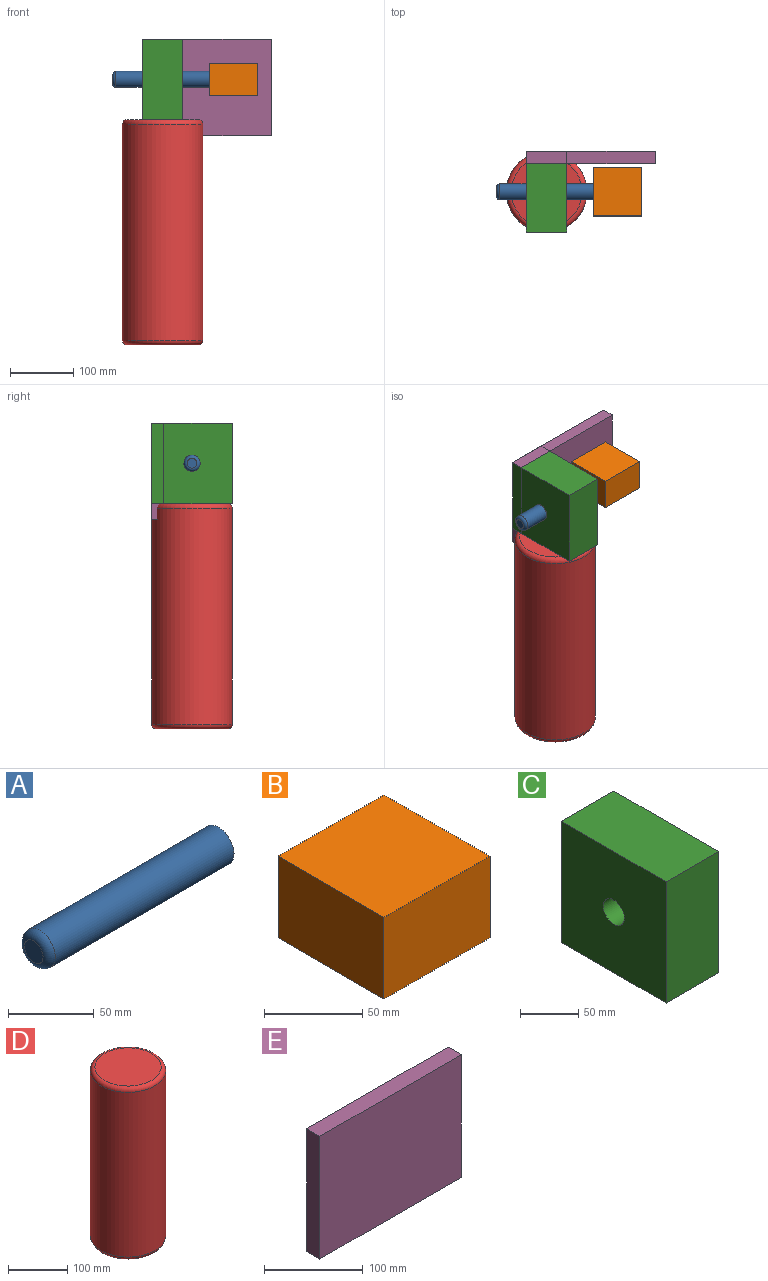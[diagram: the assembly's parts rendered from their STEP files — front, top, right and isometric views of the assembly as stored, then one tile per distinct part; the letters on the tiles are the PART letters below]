
ASSEMBLY  parts=5 mates=4
PART A: 4 faces, bbox 152.4x27.5x27.5 mm
  f0: cylinder r=12.7mm len=147.32mm, axis (-1,0,0), area 11755.6mm2, adj f1,f3
  f1: plane 25.4x25.4mm, normal (1,0,0), area 506.7mm2, adj f0
  f2: plane 15.24x15.24mm, normal (-1,0,0), area 182.4mm2, adj f3
  f3: torus R=7.62mm, axis (1,0,0), area 544.2mm2, adj f0,f2
PART B: 11 faces, bbox 76.2x76.2x50.8 mm
  f0: plane 76.2x50.8mm, normal (1,0,0), area 1703.2mm2, adj f1,f2,f4,f5,f6,f7,f8,f9
  f1: plane 76.2x76.2mm, normal (0,0,-1), area 5806.4mm2, adj f0,f3,f4,f5
  f2: plane 76.2x76.2mm, normal (0,0,1), area 5806.4mm2, adj f0,f3,f4,f5
  f3: plane 76.2x50.8mm, normal (-1,0,0), area 3871mm2, adj f1,f2,f4,f5
  f4: plane 76.2x50.8mm, normal (0,-1,0), area 3871mm2, adj f0,f1,f2,f3
  f5: plane 76.2x50.8mm, normal (0,1,0), area 3871mm2, adj f0,f1,f2,f3
  f6: plane 60.96x50.8mm, normal (0,0,1), area 3096.8mm2, adj f0,f7,f9,f10
  f7: plane 50.8x35.56mm, normal (0,-1,0), area 1806.4mm2, adj f0,f6,f8,f10
  f8: plane 60.96x50.8mm, normal (0,0,-1), area 3096.8mm2, adj f0,f7,f9,f10
  f9: plane 50.8x35.56mm, normal (0,1,0), area 1806.4mm2, adj f0,f6,f8,f10
  f10: plane 60.96x35.56mm, normal (1,0,0), area 2167.7mm2, adj f6,f7,f8,f9
PART C: 7 faces, bbox 63.5x127x127 mm
  f0: plane 127x127mm, normal (-1,0,0), area 15622.3mm2, adj f1,f3,f4,f5,f6
  f1: plane 127x63.5mm, normal (0,0,-1), area 8064.5mm2, adj f0,f2,f4,f5
  f2: plane 127x127mm, normal (1,0,0), area 15622.3mm2, adj f1,f3,f4,f5,f6
  f3: plane 127x63.5mm, normal (0,0,1), area 8064.5mm2, adj f0,f2,f4,f5
  f4: plane 127x63.5mm, normal (0,-1,0), area 8064.5mm2, adj f0,f1,f2,f3
  f5: plane 127x63.5mm, normal (0,1,0), area 8064.5mm2, adj f0,f1,f2,f3
  f6: cylinder r=12.7mm len=63.5mm, axis (1,0,0), area 5067.1mm2, adj f0,f2
PART D: 5 faces, bbox 137.5x137.5x355.6 mm
  f0: cylinder r=63.5mm len=340.36mm, axis (0,0,-1), area 135797.6mm2, adj f3,f4
  f1: plane 111.76x111.76mm, normal (0,0,1), area 9809.9mm2, adj f4
  f2: plane 111.76x111.76mm, normal (0,0,-1), area 9809.9mm2, adj f3
  f3: torus R=55.88mm, axis (0,0,1), area 4567.4mm2, adj f0,f2
  f4: torus R=55.88mm, axis (0,0,1), area 4567.4mm2, adj f0,f1
PART E: 6 faces, bbox 203.2x19.1x152.4 mm
  f0: plane 203.2x19.05mm, normal (0,0,1), area 3871mm2, adj f1,f3,f4,f5
  f1: plane 152.4x19.05mm, normal (-1,0,0), area 2903.2mm2, adj f0,f2,f4,f5
  f2: plane 203.2x19.05mm, normal (0,0,-1), area 3871mm2, adj f1,f3,f4,f5
  f3: plane 152.4x19.05mm, normal (1,0,0), area 2903.2mm2, adj f0,f2,f4,f5
  f4: plane 203.2x152.4mm, normal (0,-1,0), area 30967.7mm2, adj f0,f1,f2,f3
  f5: plane 203.2x152.4mm, normal (0,1,0), area 30967.7mm2, adj f0,f1,f2,f3
PLACE A t=(-257.06,-2.81,394.91)mm
PLACE B t=(-28.46,37.56,369.51)mm
PLACE C t=(-210.07,62.96,331.41)mm
PLACE D t=(-178.32,-0.54,-24.19)mm
PLACE E t=(-52.31,62.96,351.82)mm
MATE fastened E.f5 <-> C.f5  axis (0,1,0) through (-210.07,62.96,458.41)mm
MATE fastened C.f1 <-> D.f0  axis (0,0,-1) through (-178.32,-0.54,331.41)mm
MATE fastened B.f3 <-> A.f0  axis (-1,0,0) through (-104.66,-0.54,394.91)mm
MATE slider A.f0 <-> C.f6  axis (-1,0,0) through (-178.32,-0.54,394.91)mm
